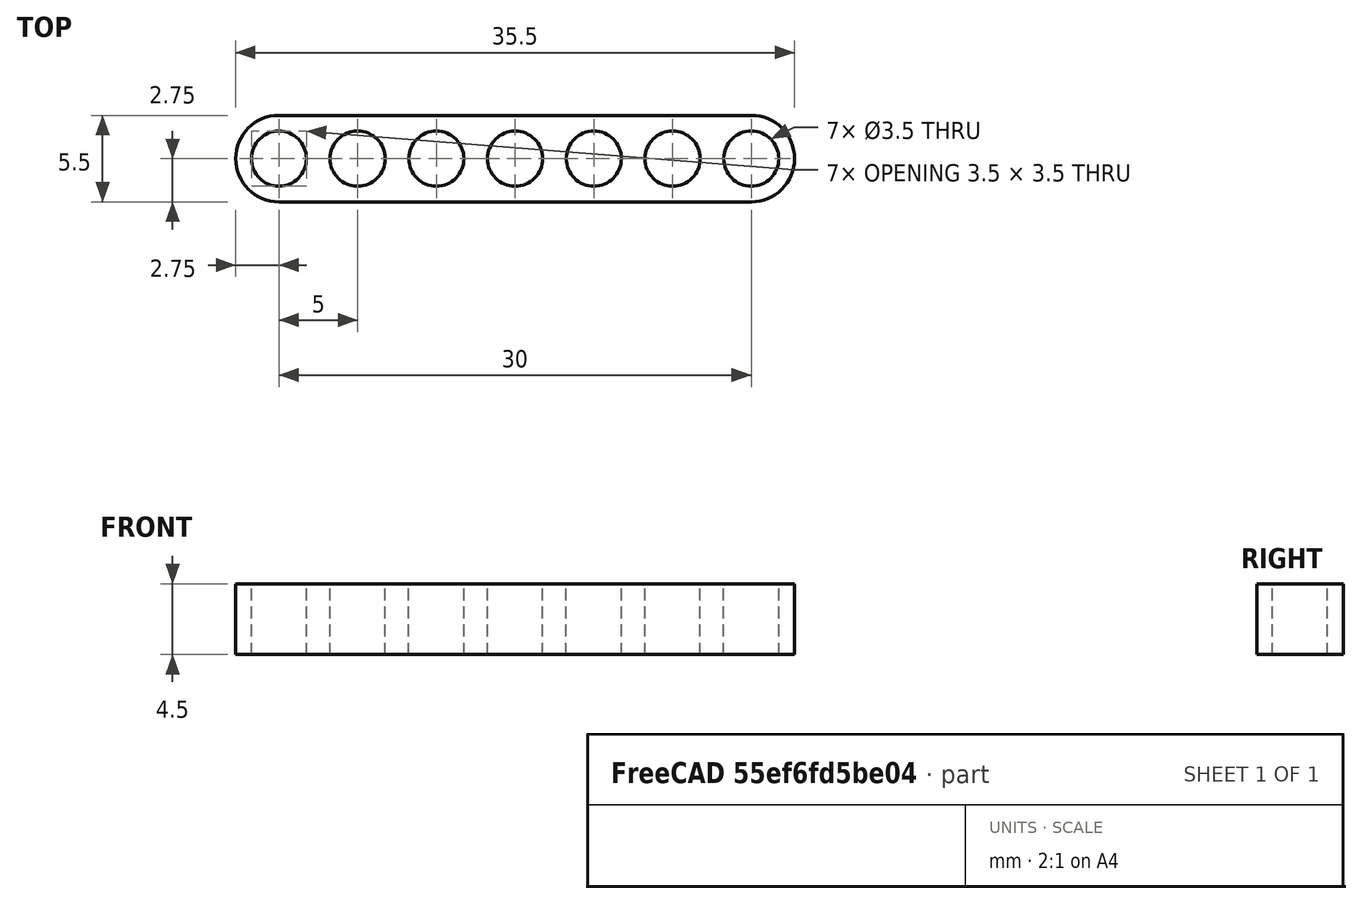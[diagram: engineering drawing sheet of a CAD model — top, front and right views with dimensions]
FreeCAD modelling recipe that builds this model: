
FCSTD DOCUMENT  (FreeCAD 0.14R3692 (Git))
Label: part
License: CC-BY 3.0
LicenseURL: http://creativecommons.org/licenses/by/3.0/
objects: Part::Cylinder×3, Part::Box×1, Part::MultiFuse×1, Part::FeaturePython×1, Part::Cut×1
note: 7 computed .brp shape members not serialized (recipe doc carries the construction recipe); baked Part::Feature solids carry a one-line shape summary decoded from their .brp

FEATURE [Part::Cylinder] Cylinder
  Angle = 360
  Height = 4.5
  Radius = 2.75
FEATURE [Part::Cylinder] Cylinder001
  Angle = 360
  Height = 4.5
  Placement = pos=(30,0,0) rot=(0,0,1;0rad)
  Radius = 2.75
FEATURE [Part::Box] Box  label="Cube"
  Height = 4.5
  Length = 30
  Placement = pos=(0,-2.75,0) rot=(0,0,1;0rad)
  Width = 5.5
FEATURE [Part::MultiFuse] Fusion
  Shapes = -> [Cylinder,Cylinder001,Box]
FEATURE [Part::Cylinder] Cylinder002
  Angle = 360
  Height = 6.5
  Placement = pos=(0,0,-1) rot=(0,0,1;0rad)
  Radius = 1.75
FEATURE [Part::FeaturePython] Array  # Draft array (typed FeaturePython)
  Angle = 360
  ArrayType = 0
  Axis = (0,0,1)
  Base = -> Cylinder002
  Center = (0,0,0)
  IntervalX = (5,0,0)
  IntervalY = (0,1,0)
  IntervalZ = (0,0,1)
  NumberPolar = 1
  NumberX = 7
  NumberY = 1
  NumberZ = 1
FEATURE [Part::Cut] Cut
  Base = -> Fusion
  Tool = -> Array
